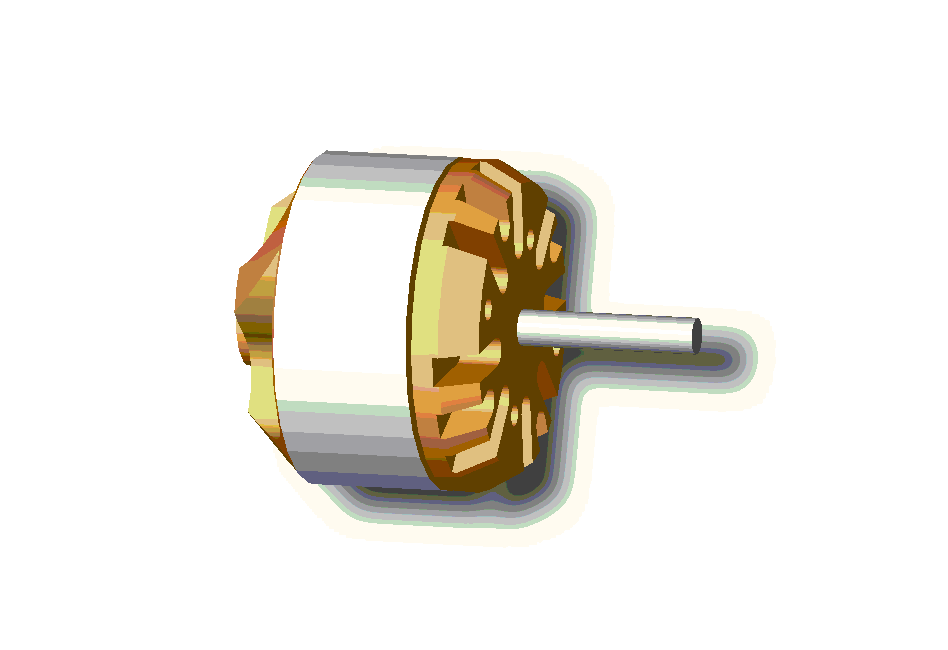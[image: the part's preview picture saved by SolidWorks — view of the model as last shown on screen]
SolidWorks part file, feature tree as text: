
SOLIDWORKS PART (.sldprt)
format: sldprt  version: not decoded by parser v0  size: 425,984 bytes
history: native  units: mm
features: sketch x9, cut_extrude x5, extrude x4, pattern_circular x4, plane x3, chamfer x2 (+8 scaffold rows collapsed)
feature tree (35):
  scaffold x8  (default folders/planes/origin — collapsed)
  sketch  "Sketch1"  dims[D1=3.88mm]
  extrude  "Base-Extrude"  Depth=48.71mm
  plane  "Plane1"  Offset=19.06mm
  sketch  "Sketch2"  dims[D1=34.9mm]
  extrude  "Boss-Extrude1"  Depth=6.7mm
  sketch  "Sketch3"  dims[D1=2.38mm D2=2.38mm D7=2.38mm D8=2.38mm D3=12.5mm D4=12.5mm D5=9.28mm D6=9.28mm]
  chamfer  "Chamfer1"  Distance=3.8mm Angle=30deg
  sketch  "Sketch4"  dims[c1.D4=34.9mm c1.D3=1.56mm c1.D1=1.56mm c1.D2=3.12mm c2.D3=~23.438864mm c3.D3=45.0deg c3.D4=~7.905095mm c3.D5=12.91mm c3.D1=~9.128749mm c4.D3=~9.128749mm c4.D6=~4.470129mm c4.D1=36.75mm c5.D1=45.0deg]
  cut_extrude  "Cut-Extrude3"  [1 undecoded]
  cut_extrude  "Cut-Extrude4"  Depth=4.4mm
  pattern_circular  "CirPattern1"  Count=4 Angle=91deg
  sketch  "Sketch5"  dims[c1.D1=3.1mm c1.D4=3.1mm c1.D2=~2.266101mm c2.D2=20.0deg c2.D3=~2.266101mm c3.D3=20.0deg c3.D5=9.0mm c3.D6=9.0mm c3.D7=9.0mm c3.D8=9.0mm c3.D9=~6.156363mm c3.D10=9.0mm c4.D10=40.0deg c5.D10=~2.266101mm c6.D10=67.0deg c7.D10=~3.965948mm c7.D11=~9.824675mm]
  cut_extrude  "Cut-Extrude5"  [1 undecoded]
  pattern_circular  "CirPattern2"  Count=4 Angle=90deg
  plane  "Plane2"  Offset=0.6mm
  plane  "Plane3"  Offset=1.64mm
  sketch  "Sketch6"  dims[D1=35.0mm]
  extrude  "Boss-Extrude3"  [1 undecoded]
  chamfer  "Chamfer2"  Distance=6.26mm
  sketch  "Sketch7"  dims[D1=10.81mm D2=3.88mm]
  extrude  "Boss-Extrude4"  Depth=1.6mm
  sketch  "Sketch8"  dims[D2=2.0mm D1=7.46mm]
  cut_extrude  "Cut-Extrude6"  Depth=4mm
  pattern_circular  "CirPattern3"  Count=4 Angle=90deg
  sketch  "Sketch9"  dims[c1.D1=11.0mm c1.D4=~30.432523mm c1.D2=~8.649472mm c1.D3=~12.247657mm c2.D4=~11.796823mm]
  cut_extrude  "Cut-Extrude7"  Depth=6mm
  pattern_circular  "CirPattern4"  Count=4 Angle=90deg
decode coverage: 21 of 24 modeling features carry decoded parameters
note: ~ marks probable driven/reference dimensions
note: 3 parameter values undecoded
summary: no parameter record found for 3 features
note: suppression state not decoded; provenance and decode notes live in map.json
